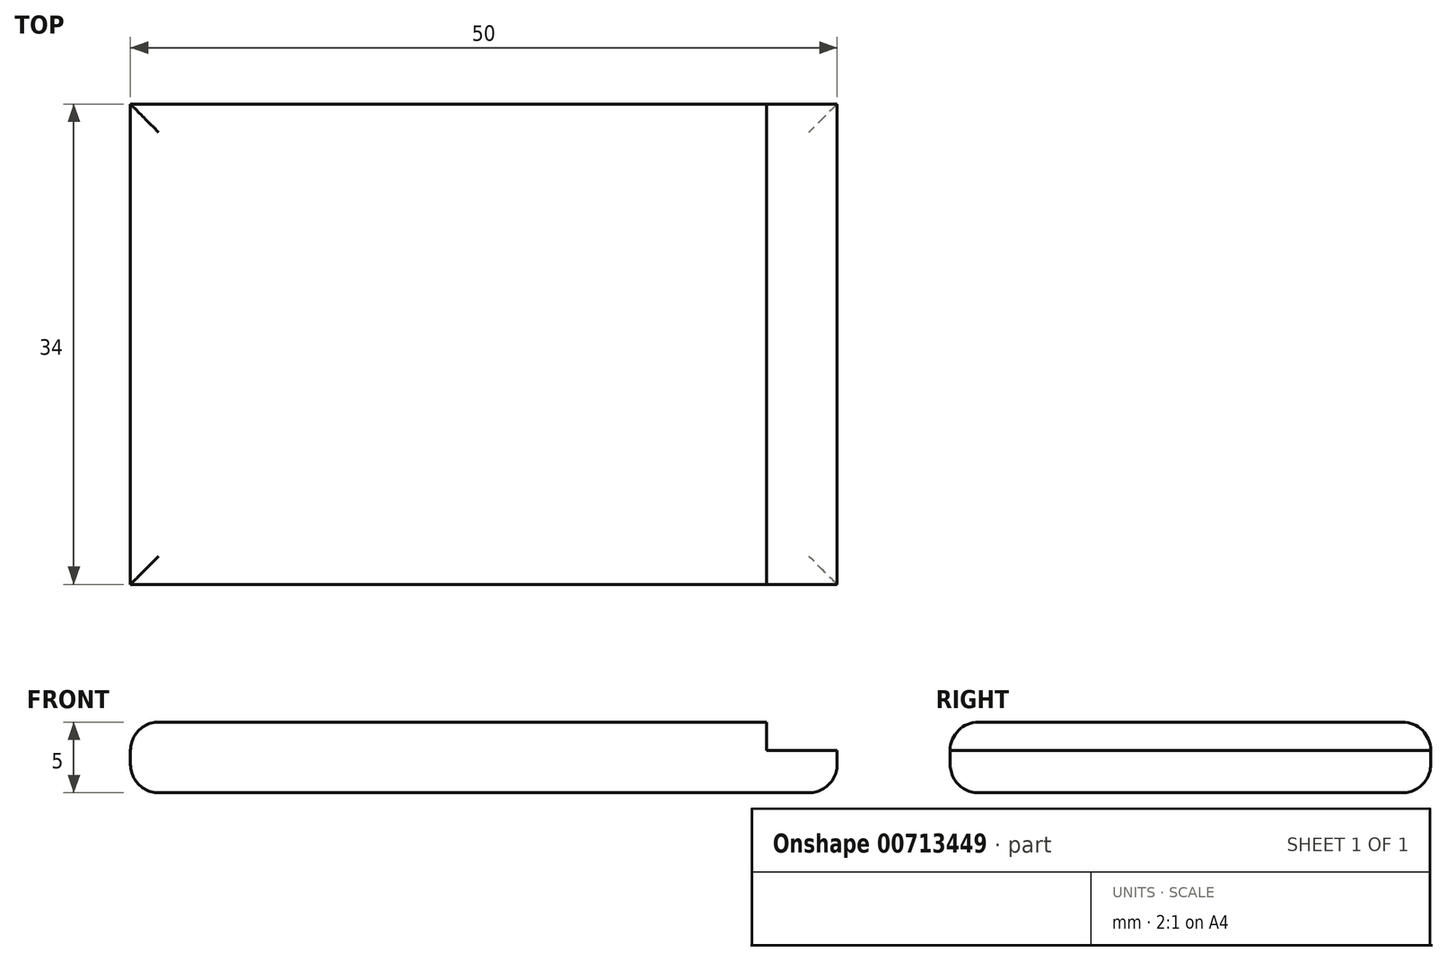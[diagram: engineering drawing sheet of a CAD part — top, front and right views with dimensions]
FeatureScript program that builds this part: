
annotation { "Feature Type Name" : "Feature", "Feature Type Description" : "" }
export const myFeature = defineFeature(function(context is Context, id is Id, definition is map)
    precondition{}
    {
        {
            var Q0;
            Q0=qCreatedBy(makeId("Top.planeOp"),FACE);
            var sketch = newSketch(context, id + "F0", { "sketchPlane" : qUnion([Q0])});
            skLineSegment(sketch, "E0.bottom", {"start": v(25, 17) * mm, "end": v(-25, 17) * mm});
            skLineSegment(sketch, "E0.top", {"start": v(25, -17) * mm, "end": v(-25, -17) * mm});
            skLineSegment(sketch, "E0.left", {"start": v(25, 17) * mm, "end": v(25, -17) * mm});
            skLineSegment(sketch, "E0.right", {"start": v(-25, 17) * mm, "end": v(-25, -17) * mm});
            skPoint(sketch, "E0.middle", {"position": v(0, 0) * mm});
            skSolve(sketch);
        }
        {
            var Q0;
            Q0 = qSketchRegion(id + "F0", true);
            extrude(context, id + "F1", {"entities" : qUnion([Q0]), "depth" : 5 * mm, "offsetDistance" : 25 * mm});
        }
        {
            var Q0;
            Q0=makeQuery(id+"F1.opExtrude","CAP_FACE",FACE,{"disambiguationData":[OSD([sQuery(id+"F0.wireOp",EDGE,"E0.bottom"),sQuery(id+"F0.wireOp",EDGE,"E0.top"),sQuery(id+"F0.wireOp",EDGE,"E0.left"),sQuery(id+"F0.wireOp",EDGE,"E0.right")])],"isStart":false});
            var sketch = newSketch(context, id + "F2", { "sketchPlane" : qUnion([Q0])});
            skLineSegment(sketch, "E1.bottom", {"start": v(25, -17) * mm, "end": v(20, -17) * mm});
            skLineSegment(sketch, "E1.top", {"start": v(25, 17) * mm, "end": v(20, 17) * mm});
            skLineSegment(sketch, "E1.left", {"start": v(25, -17) * mm, "end": v(25, 17) * mm});
            skLineSegment(sketch, "E1.right", {"start": v(20, -17) * mm, "end": v(20, 17) * mm});
            skSolve(sketch);
        }
        {
            var Q0;
            Q0 = qSketchRegion(id + "F2", true);
            extrude(context, id + "F3", {"entities" : qUnion([Q0]), "operationType" : NewBodyOperationType.REMOVE, "oppositeDirection" : true, "depth" : 2 * mm, "offsetDistance" : 25 * mm});
        }
        {
            var Q0;
            Q0=makeQuery(id+"F1.opExtrude","CAP_EDGE",EDGE,{"disambiguationData":[OSD([sQuery(id+"F0.wireOp",EDGE,"E0.bottom")])],"isStart":false});
            var Q1;
            Q1=makeQuery(id+"F1.opExtrude","CAP_EDGE",EDGE,{"disambiguationData":[OSD([sQuery(id+"F0.wireOp",EDGE,"E0.top")])],"isStart":false});
            var Q2;
            Q2=makeQuery(id+"F1.opExtrude","CAP_EDGE",EDGE,{"disambiguationData":[OSD([sQuery(id+"F0.wireOp",EDGE,"E0.top")])],"isStart":true});
            var Q3;
            Q3=makeQuery(id+"F1.opExtrude","CAP_EDGE",EDGE,{"disambiguationData":[OSD([sQuery(id+"F0.wireOp",EDGE,"E0.bottom")])],"isStart":true});
            var Q4;
            Q4=makeQuery(id+"F1.opExtrude","CAP_EDGE",EDGE,{"disambiguationData":[OSD([sQuery(id+"F0.wireOp",EDGE,"E0.right")])],"isStart":true});
            var Q5;
            Q5=makeQuery(id+"F1.opExtrude","CAP_EDGE",EDGE,{"disambiguationData":[OSD([sQuery(id+"F0.wireOp",EDGE,"E0.right")])],"isStart":false});
            var Q6;
            Q6=makeQuery(id+"F1.opExtrude","CAP_EDGE",EDGE,{"disambiguationData":[OSD([sQuery(id+"F0.wireOp",EDGE,"E0.left")])],"isStart":true});
            fillet(context, id + "F4", {"entities" : qUnion([Q0, Q1, Q2, Q3, Q4, Q5, Q6]), "radius" : 2 * mm, "tangentPropagation" : true, "allowEdgeOverflow" : false});
        }
    });
